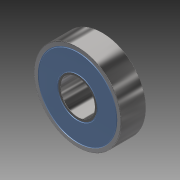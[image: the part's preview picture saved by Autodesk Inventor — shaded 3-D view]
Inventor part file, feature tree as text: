
AUTODESK INVENTOR PART (.ipt)
format: ipt  version: 2014 (Build 180170000, 170)  size: 173,056 bytes
history: native  units: in
note: dims shown in document units (in); Inventor stores cm internally (conversion verified against a paired STEP export)
features: sketch x2, extrude x1, fillet x1, revolve x1, plane x1, mirror x1
ambient origin geometry x8: Origin, YZ Plane, XZ Plane, XY Plane, X Axis, Y Axis, Z Axis, Center Point
bodies: Solid1 (feature_tree)
feature tree (7):
  extrude  "Extrusion1"  Depth=0.6299in
  fillet  "Fillet1"  Radius=0.6299in
  revolve  "Revolution1"  Angle=90.0deg
  plane  "Work Plane1"
  mirror  "Mirror1"
  sketch  "Sketch1"  dims[d0=0.8661in d1=2.2047in d2=0.6299in d3=0.0in]
  sketch  "Sketch2"  dims[d4=0.0118in d5=90.0deg]
